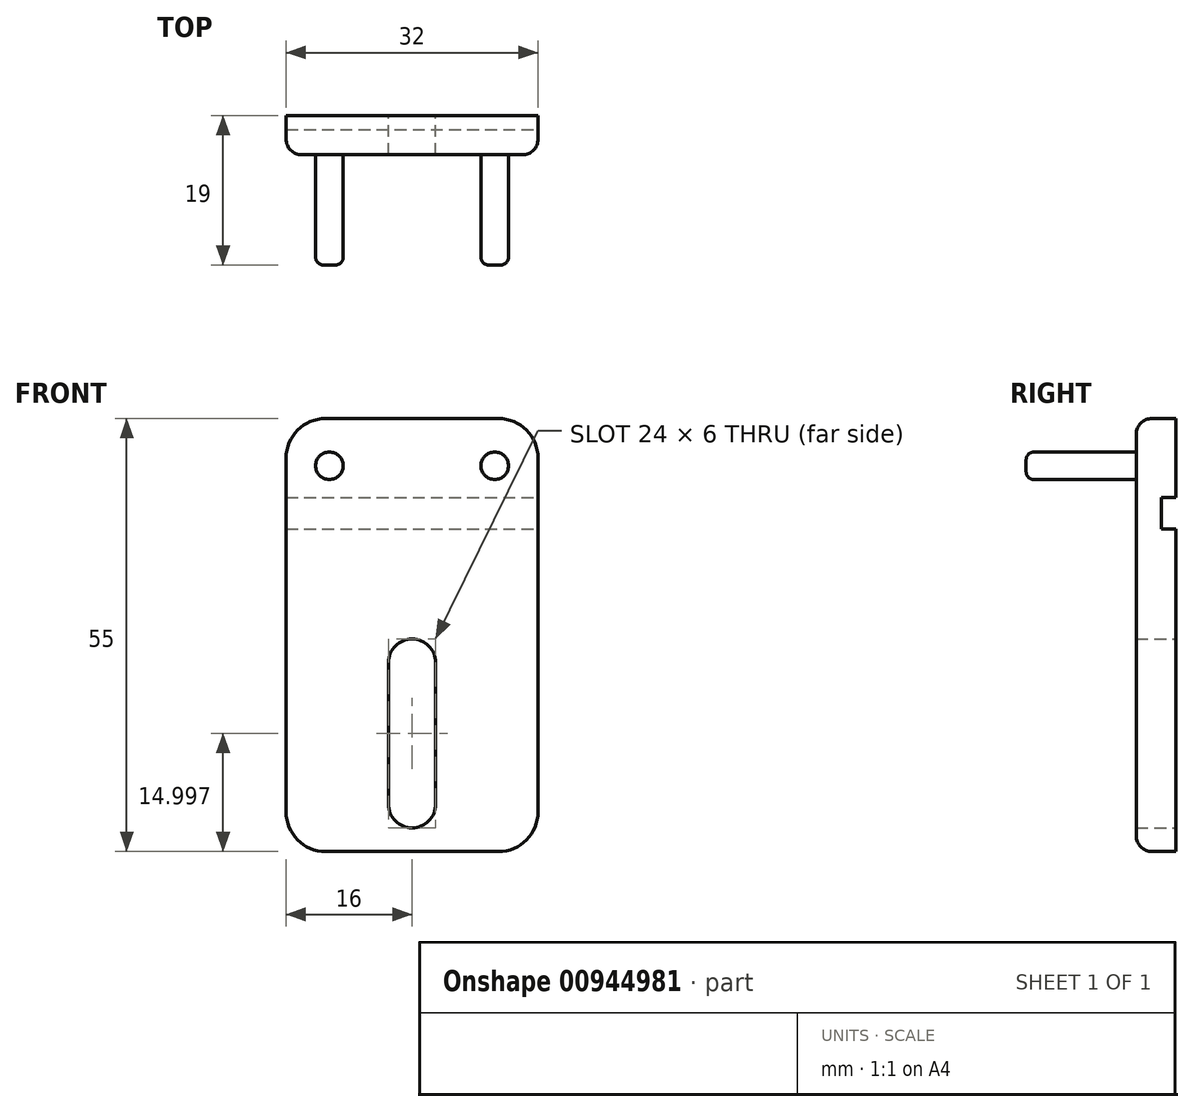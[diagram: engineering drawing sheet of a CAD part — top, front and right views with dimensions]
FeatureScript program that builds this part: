
annotation { "Feature Type Name" : "Feature", "Feature Type Description" : "" }
export const myFeature = defineFeature(function(context is Context, id is Id, definition is map)
    precondition{}
    {
        {
            var Q0;
            Q0=qCreatedBy(makeId("Front.planeOp"),FACE);
            var sketch = newSketch(context, id + "F0", { "sketchPlane" : qUnion([Q0])});
            skLineSegment(sketch, "E0.bottom", {"start": v(-129.4, 18.95) * mm, "end": v(-97.4, 18.95) * mm});
            skLineSegment(sketch, "E0.top", {"start": v(-129.4, -36.05) * mm, "end": v(-97.4, -36.05) * mm});
            skLineSegment(sketch, "E0.left", {"start": v(-129.4, 18.95) * mm, "end": v(-129.4, -36.05) * mm});
            skLineSegment(sketch, "E0.right", {"start": v(-97.4, 18.95) * mm, "end": v(-97.4, -36.05) * mm});
            skSolve(sketch);
        }
        {
            var Q0;
            Q0=makeQuery(id+"F0.imprint","IMPRINT",FACE,{"disambiguationData":[TD([[makeQuery(id+"F0.imprint","IMPRINT",EDGE,{"derivedFrom":sQuery(id+"F0.wireOp",EDGE,"E0.bottom")}),-1.0]])]});
            var sketch = newSketch(context, id + "F1", { "sketchPlane" : qUnion([Q0])});
            skCircle(sketch, "E1", {"center": v(-123.9, 12.95) * mm, "radius": 1.75 * mm});
            skCircle(sketch, "E2", {"center": v(-102.9, 12.95) * mm, "radius": 1.75 * mm});
            skLineSegment(sketch, "E3", {"start": v(-123.9, 12.95) * mm, "end": v(-102.9, 12.95) * mm, "construction": true});
            skPoint(sketch, "E4", {"position": v(-113.4, 12.95) * mm});
            skPoint(sketch, "E5", {"position": v(-113.4, 18.95) * mm});
            skSolve(sketch);
        }
        {
            var Q0;
            Q0=makeQuery(id+"F0.imprint","IMPRINT",FACE,{"disambiguationData":[TD([[makeQuery(id+"F0.imprint","IMPRINT",EDGE,{"derivedFrom":sQuery(id+"F0.wireOp",EDGE,"E0.bottom")}),-1.0]])]});
            var sketch = newSketch(context, id + "F2", { "sketchPlane" : qUnion([Q0])});
            skCircle(sketch, "E6", {"center": v(-113.4, -12.05) * mm, "radius": 3 * mm});
            skCircle(sketch, "E7", {"center": v(-113.4, -30.05) * mm, "radius": 3 * mm});
            skPoint(sketch, "E8", {"position": v(-113.4, -36.05) * mm});
            skLineSegment(sketch, "E9", {"start": v(-110.4, -12.05) * mm, "end": v(-110.4, -30.05) * mm});
            skLineSegment(sketch, "E10", {"start": v(-116.4, -30.05) * mm, "end": v(-116.4, -12.05) * mm});
            skPoint(sketch, "E11", {"position": v(-113.4, 12.95) * mm});
            skSolve(sketch);
        }
        {
            var Q0;
            Q0 = qSketchRegion(id + "F0", true);
            extrude(context, id + "F3", {"entities" : qUnion([Q0]), "depth" : 5 * mm, "offsetDistance" : 25 * mm});
        }
        {
            var Q0;
            Q0 = qSketchRegion(id + "F1", true);
            extrude(context, id + "F4", {"entities" : qUnion([Q0]), "operationType" : NewBodyOperationType.ADD, "depth" : (13 + 6) * mm, "offsetDistance" : 25 * mm});
        }
        {
            var Q0;
            Q0 = qSketchRegion(id + "F2", true);
            extrude(context, id + "F5", {"entities" : qUnion([Q0]), "operationType" : NewBodyOperationType.REMOVE, "depth" : 5 * mm, "offsetDistance" : 25 * mm});
        }
        {
            var Q0;
            Q0=qCreatedBy(makeId("Front.planeOp"),FACE);
            var sketch = newSketch(context, id + "F6", { "sketchPlane" : qUnion([Q0])});
            skLineSegment(sketch, "E12.bottom", {"start": v(-134.25, 8.95) * mm, "end": v(-84.25, 8.95) * mm});
            skLineSegment(sketch, "E12.top", {"start": v(-134.25, 4.95) * mm, "end": v(-84.25, 4.95) * mm});
            skLineSegment(sketch, "E12.left", {"start": v(-134.25, 8.95) * mm, "end": v(-134.25, 4.95) * mm});
            skLineSegment(sketch, "E12.right", {"start": v(-84.25, 8.95) * mm, "end": v(-84.25, 4.95) * mm});
            skLineSegment(sketch, "E13.bottom", {"start": v(-134.25, 8.95) * mm, "end": v(-134.25, 8.95) * mm});
            skLineSegment(sketch, "E13.top", {"start": v(-134.25, 4.95) * mm, "end": v(-134.25, 4.95) * mm});
            skPoint(sketch, "E14", {"position": v(-109.25, 8.95) * mm});
            skSolve(sketch);
        }
        {
            var Q0;
            Q0 = qSketchRegion(id + "F6", true);
            extrude(context, id + "F7", {"entities" : qUnion([Q0]), "operationType" : NewBodyOperationType.REMOVE, "depth" : 1.8 * mm, "offsetDistance" : 25 * mm});
        }
        {
            var Q0;
            Q0=makeQuery(id+"F3.opExtrude","SWEPT_EDGE",EDGE,{"disambiguationData":[OSD([sQuery(id+"F0.wireOp",EDGE,"E0.bottom"),sQuery(id+"F0.wireOp",EDGE,"E0.right")])]});
            fillet(context, id + "F8", {"entities" : qUnion([Q0]), "radius" : 5 * mm, "tangentPropagation" : true, "allowEdgeOverflow" : false});
        }
        {
            var Q0;
            Q0=makeQuery(id+"F3.opExtrude","SWEPT_EDGE",EDGE,{"disambiguationData":[OSD([sQuery(id+"F0.wireOp",EDGE,"E0.bottom"),sQuery(id+"F0.wireOp",EDGE,"E0.left")])]});
            fillet(context, id + "F9", {"entities" : qUnion([Q0]), "radius" : 5 * mm, "tangentPropagation" : true, "allowEdgeOverflow" : false});
        }
        {
            var Q0;
            Q0=makeQuery(id+"F3.opExtrude","SWEPT_EDGE",EDGE,{"disambiguationData":[OSD([sQuery(id+"F0.wireOp",EDGE,"E0.top"),sQuery(id+"F0.wireOp",EDGE,"E0.left")])]});
            fillet(context, id + "F10", {"entities" : qUnion([Q0]), "radius" : 5 * mm, "tangentPropagation" : true, "allowEdgeOverflow" : false});
        }
        {
            var Q0;
            Q0=makeQuery(id+"F3.opExtrude","SWEPT_EDGE",EDGE,{"disambiguationData":[OSD([sQuery(id+"F0.wireOp",EDGE,"E0.top"),sQuery(id+"F0.wireOp",EDGE,"E0.right")])]});
            fillet(context, id + "F11", {"entities" : qUnion([Q0]), "radius" : 5 * mm, "tangentPropagation" : true, "allowEdgeOverflow" : false});
        }
        {
            var Q0;
            {var subQ0=sQuery(id+"F0.wireOp",EDGE,"E0.right");var subQ1=sQuery(id+"F0.wireOp",EDGE,"E0.bottom");Q0=makeQuery(id+"F8.opFillet","BLEND_EDGE",EDGE,{"blendedFrom":[makeQuery(id+"F3.opExtrude","SWEPT_EDGE",EDGE,{"disambiguationData":[OSD([subQ1,subQ0])]}),makeQuery(id+"F3.opExtrude","CAP_FACE",FACE,{"disambiguationData":[OSD([subQ1,sQuery(id+"F0.wireOp",EDGE,"E0.top"),sQuery(id+"F0.wireOp",EDGE,"E0.left"),subQ0])],"isStart":false})],"blendedInto":[makeQuery(id+"F3.opExtrude","CAP_FACE",FACE,{"disambiguationData":[OSD([subQ1,sQuery(id+"F0.wireOp",EDGE,"E0.top"),sQuery(id+"F0.wireOp",EDGE,"E0.left"),subQ0])],"isStart":false})]});}
            var Q1;
            Q1=makeQuery(id+"F3.opExtrude","CAP_EDGE",EDGE,{"disambiguationData":[OSD([sQuery(id+"F0.wireOp",EDGE,"E0.bottom")])],"isStart":false});
            var Q2;
            {var subQ0=sQuery(id+"F0.wireOp",EDGE,"E0.left");var subQ1=sQuery(id+"F0.wireOp",EDGE,"E0.bottom");Q2=makeQuery(id+"F9.opFillet","BLEND_EDGE",EDGE,{"blendedFrom":[makeQuery(id+"F3.opExtrude","SWEPT_EDGE",EDGE,{"disambiguationData":[OSD([subQ1,subQ0])]}),makeQuery(id+"F3.opExtrude","CAP_FACE",FACE,{"disambiguationData":[OSD([subQ1,sQuery(id+"F0.wireOp",EDGE,"E0.top"),subQ0,sQuery(id+"F0.wireOp",EDGE,"E0.right")])],"isStart":false})],"blendedInto":[makeQuery(id+"F3.opExtrude","CAP_FACE",FACE,{"disambiguationData":[OSD([subQ1,sQuery(id+"F0.wireOp",EDGE,"E0.top"),subQ0,sQuery(id+"F0.wireOp",EDGE,"E0.right")])],"isStart":false})]});}
            var Q3;
            Q3=makeQuery(id+"F3.opExtrude","CAP_EDGE",EDGE,{"disambiguationData":[OSD([sQuery(id+"F0.wireOp",EDGE,"E0.left")])],"isStart":false});
            var Q4;
            {var subQ0=sQuery(id+"F0.wireOp",EDGE,"E0.left");var subQ1=sQuery(id+"F0.wireOp",EDGE,"E0.top");Q4=makeQuery(id+"F10.opFillet","BLEND_EDGE",EDGE,{"blendedFrom":[makeQuery(id+"F3.opExtrude","SWEPT_EDGE",EDGE,{"disambiguationData":[OSD([subQ1,subQ0])]}),makeQuery(id+"F3.opExtrude","CAP_FACE",FACE,{"disambiguationData":[OSD([sQuery(id+"F0.wireOp",EDGE,"E0.bottom"),subQ1,subQ0,sQuery(id+"F0.wireOp",EDGE,"E0.right")])],"isStart":false})],"blendedInto":[makeQuery(id+"F3.opExtrude","CAP_FACE",FACE,{"disambiguationData":[OSD([sQuery(id+"F0.wireOp",EDGE,"E0.bottom"),subQ1,subQ0,sQuery(id+"F0.wireOp",EDGE,"E0.right")])],"isStart":false})]});}
            var Q5;
            Q5=makeQuery(id+"F3.opExtrude","CAP_EDGE",EDGE,{"disambiguationData":[OSD([sQuery(id+"F0.wireOp",EDGE,"E0.top")])],"isStart":false});
            var Q6;
            Q6=makeQuery(id+"F3.opExtrude","CAP_EDGE",EDGE,{"disambiguationData":[OSD([sQuery(id+"F0.wireOp",EDGE,"E0.right")])],"isStart":false});
            fillet(context, id + "F12", {"entities" : qUnion([Q0, Q1, Q2, Q3, Q4, Q5, Q6]), "radius" : 2 * mm, "tangentPropagation" : true, "allowEdgeOverflow" : false});
        }
        {
            var Q0;
            Q0=makeQuery(id+"F4.opExtrude","CAP_EDGE",EDGE,{"disambiguationData":[OSD([sQuery(id+"F1.wireOp",EDGE,"E1")])],"isStart":false});
            var Q1;
            Q1=makeQuery(id+"F4.opExtrude","CAP_EDGE",EDGE,{"disambiguationData":[OSD([sQuery(id+"F1.wireOp",EDGE,"E2")])],"isStart":false});
            fillet(context, id + "F13", {"entities" : qUnion([Q0, Q1]), "radius" : 1 * mm, "tangentPropagation" : true, "allowEdgeOverflow" : false});
        }
    });
